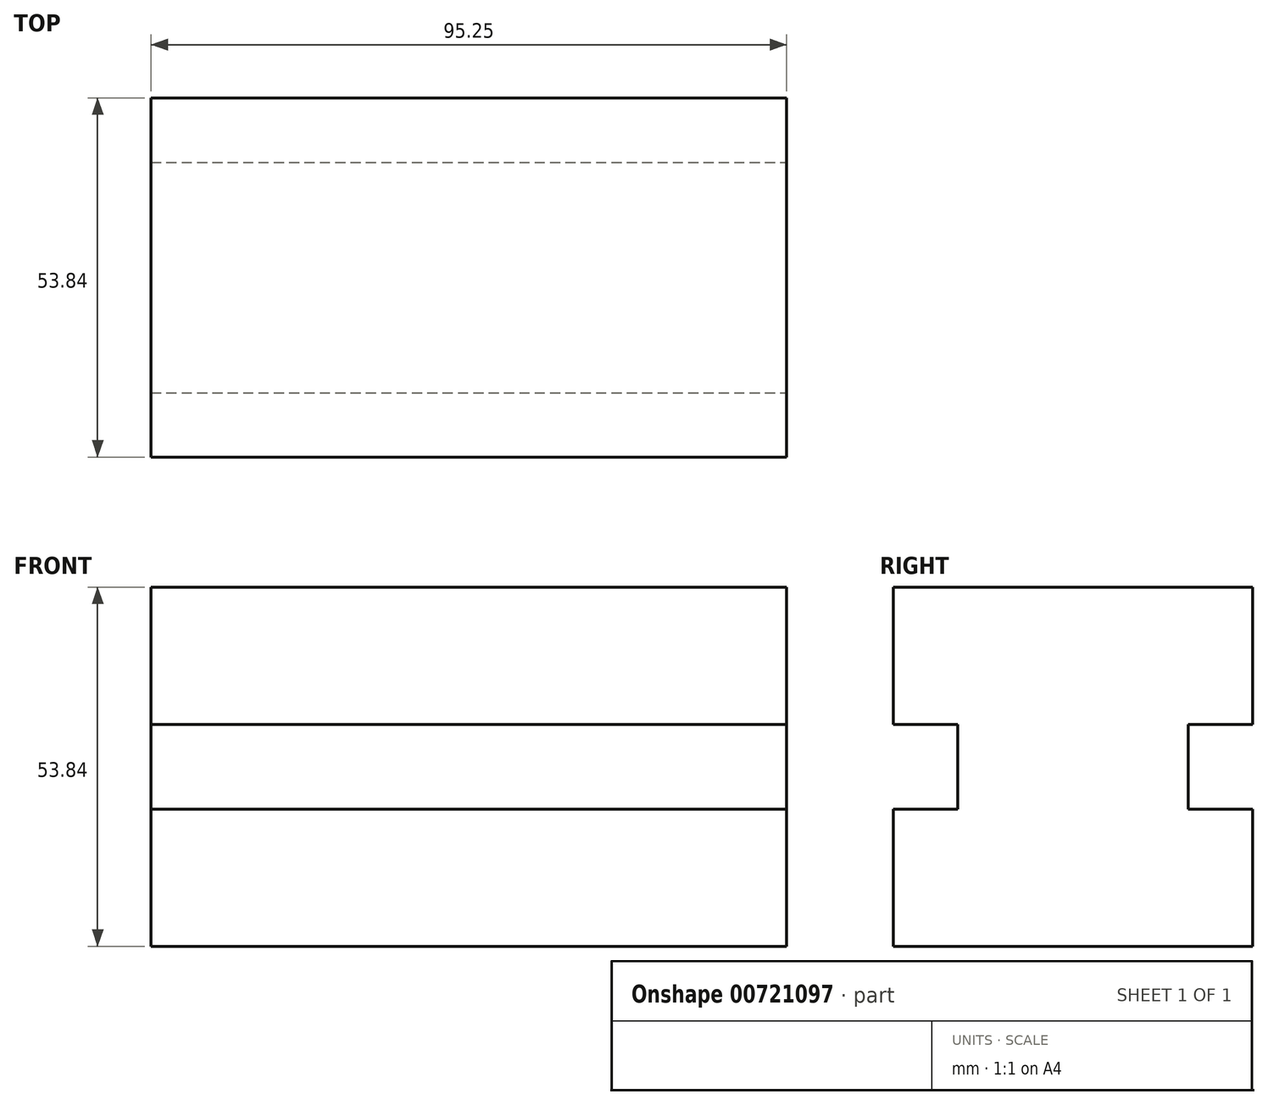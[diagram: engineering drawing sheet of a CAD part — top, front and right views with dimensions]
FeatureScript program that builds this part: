
annotation { "Feature Type Name" : "Feature", "Feature Type Description" : "" }
export const myFeature = defineFeature(function(context is Context, id is Id, definition is map)
    precondition{}
    {
        {
            var Q0;
            Q0=qCreatedBy(makeId("Right.planeOp"),FACE);
            var sketch = newSketch(context, id + "F0", { "sketchPlane" : qUnion([Q0])});
            skLineSegment(sketch, "E0.bottom", {"start": v(-26.92, 26.92) * mm, "end": v(26.92, 26.92) * mm});
            skLineSegment(sketch, "E0.top", {"start": v(-26.92, -26.92) * mm, "end": v(26.92, -26.92) * mm});
            skLineSegment(sketch, "E0.left", {"start": v(-26.92, 26.92) * mm, "end": v(-26.92, 6.35) * mm});
            skLineSegment(sketch, "E0.right", {"start": v(26.92, 26.92) * mm, "end": v(26.92, 6.35) * mm});
            skPoint(sketch, "E0.middle", {"position": v(0, 0) * mm});
            skLineSegment(sketch, "E1.bottom", {"start": v(-26.92, 6.35) * mm, "end": v(-17.27, 6.35) * mm});
            skLineSegment(sketch, "E1.top", {"start": v(-26.92, -6.35) * mm, "end": v(-17.27, -6.35) * mm});
            skLineSegment(sketch, "E1.right", {"start": v(-17.27, 6.35) * mm, "end": v(-17.27, -6.35) * mm});
            skLineSegment(sketch, "E2", {"start": v(0, 34.85) * mm, "end": v(0, -41.44) * mm, "construction": true});
            skPoint(sketch, "E2.startSnap0", {"position": v(0, 26.92) * mm});
            skLineSegment(sketch, "E3.MirrorCS", {"start": v(26.92, -6.35) * mm, "end": v(17.27, -6.35) * mm});
            skLineSegment(sketch, "E4.MirrorCS", {"start": v(17.27, 6.35) * mm, "end": v(17.27, -6.35) * mm});
            skLineSegment(sketch, "E5.MirrorCS", {"start": v(26.92, 6.35) * mm, "end": v(17.27, 6.35) * mm});
            skLineSegment(sketch, "E6.trimOffspring", {"start": v(-26.92, -6.35) * mm, "end": v(-26.92, -26.92) * mm});
            skLineSegment(sketch, "E7.trimOffspring", {"start": v(26.92, -6.35) * mm, "end": v(26.92, -26.92) * mm});
            skSolve(sketch);
        }
        {
            var Q0;
            Q0=makeQuery(id+"F0.imprint","IMPRINT",FACE,{"disambiguationData":[TD([[makeQuery(id+"F0.imprint","IMPRINT",EDGE,{"derivedFrom":sQuery(id+"F0.wireOp",EDGE,"E0.bottom")}),-1.0]])]});
            extrude(context, id + "F1", {"entities" : qUnion([Q0]), "oppositeDirection" : true, "depth" : 95.25 * mm, "offsetDistance" : 25.4 * mm});
        }
    });
